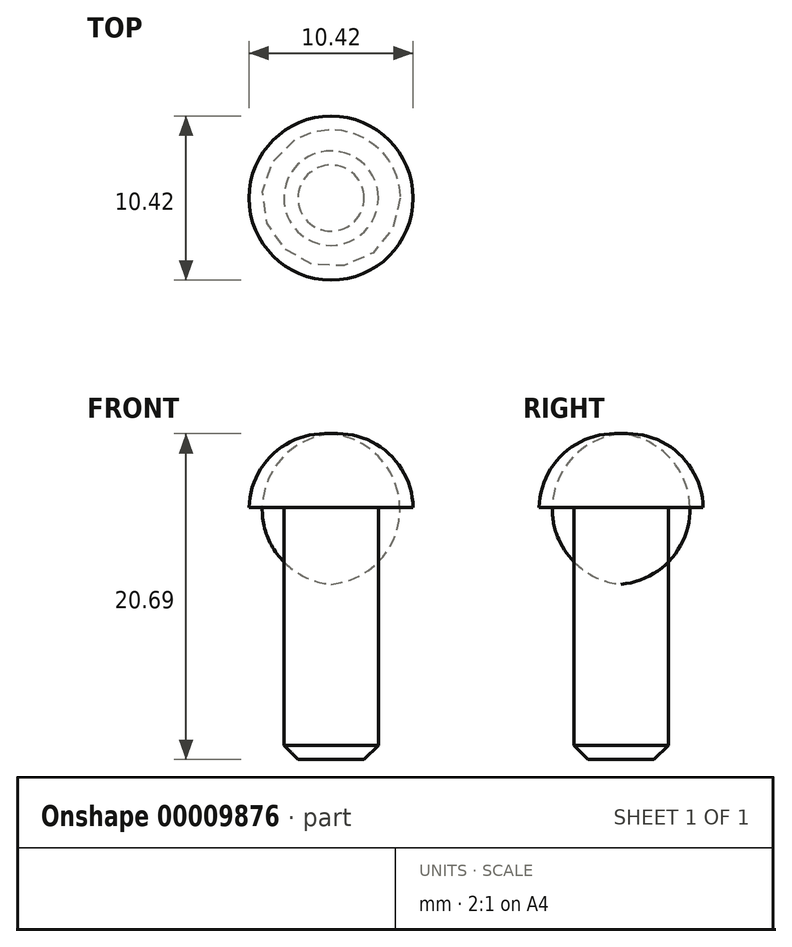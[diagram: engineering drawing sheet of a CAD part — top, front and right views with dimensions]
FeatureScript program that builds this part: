
annotation { "Feature Type Name" : "Feature", "Feature Type Description" : "" }
export const myFeature = defineFeature(function(context is Context, id is Id, definition is map)
    precondition{}
    {
        {
            var Q0;
            Q0=qCreatedBy(makeId("Front.planeOp"),FACE);
            var sketch = newSketch(context, id + "F0", { "sketchPlane" : qUnion([Q0])});
            skLineSegment(sketch, "E0", {"start": v(0, -8.06) * mm, "end": v(2.1, -8.06) * mm});
            skLineSegment(sketch, "E1", {"start": v(2.1, -8.06) * mm, "end": v(3, -7.16) * mm});
            skLineSegment(sketch, "E2", {"start": v(3, -7.16) * mm, "end": v(3, 7.94) * mm});
            skLineSegment(sketch, "E3", {"start": v(0, 7.94) * mm, "end": v(5.2, 7.94) * mm});
            skArc(sketch, "E4", {"start": v(5.2, 7.94) * mm, "mid": v(3.62, 11.4) * mm, "end": v(0, 12.61) * mm});
            skLineSegment(sketch, "E5", {"start": v(0, -8.06) * mm, "end": v(0, 7.94) * mm});
            skLineSegment(sketch, "E6", {"start": v(0, 7.94) * mm, "end": v(0, 12.61) * mm});
            skSolve(sketch);
        }
        {
            var Q0;
            Q0 = qSketchRegion(id + "F0", true);
            var Q1;
            Q1=sQuery(id+"F0.wireOp",EDGE,"E5");
            revolve(context, id + "F1", {"entities" : qUnion([Q0]), "axis" : qUnion([Q1]), "revolveType" : RevolveType.FULL});
        }
    });
